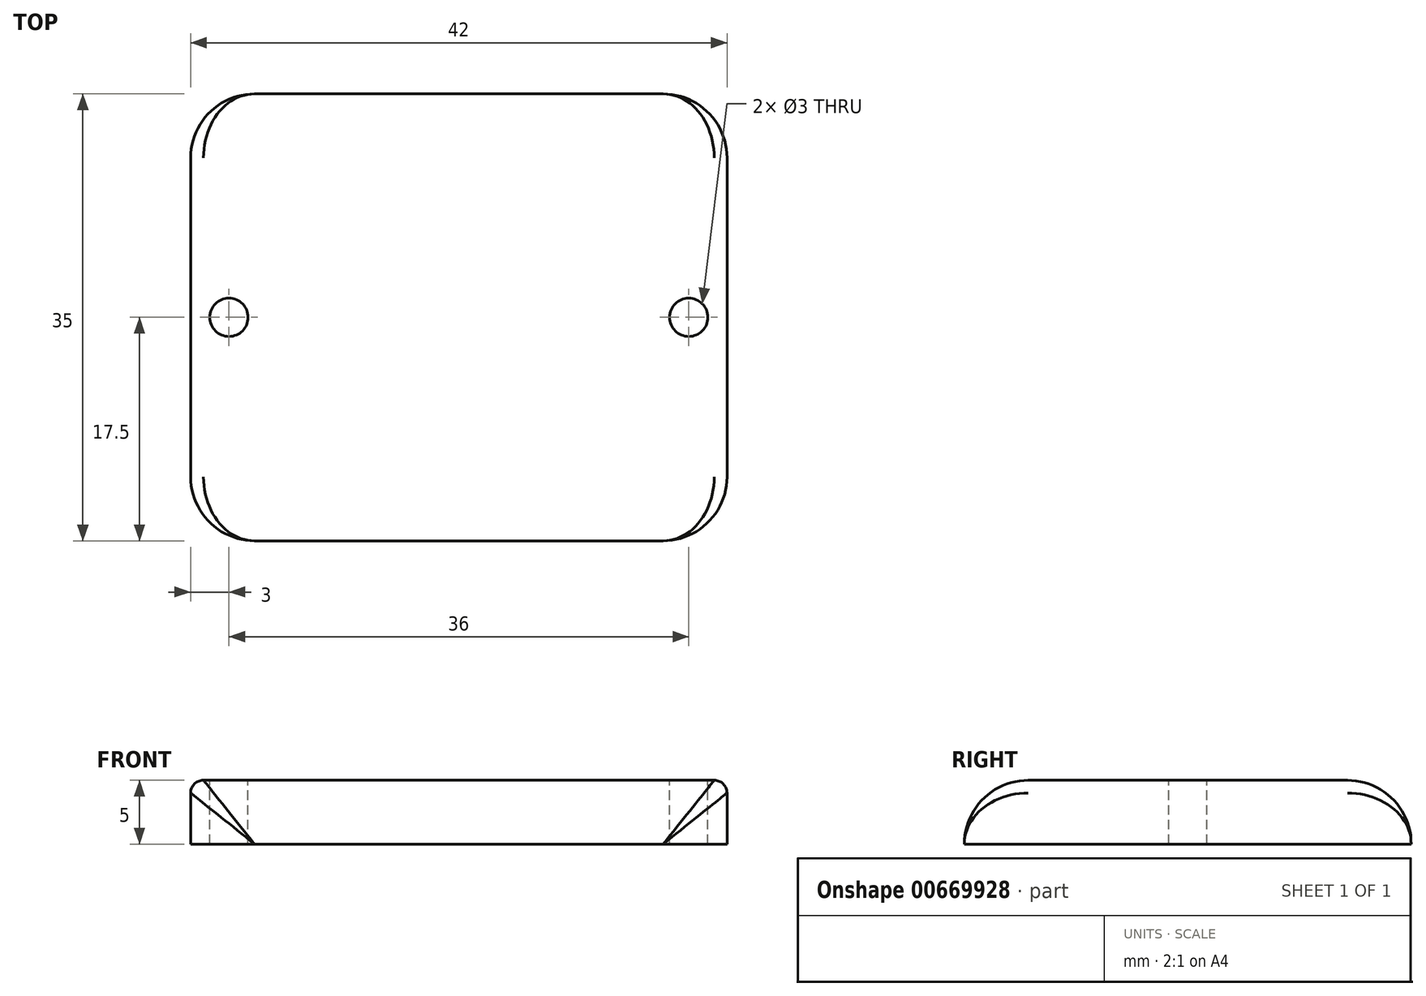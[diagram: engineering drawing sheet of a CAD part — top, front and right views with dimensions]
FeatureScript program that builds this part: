
annotation { "Feature Type Name" : "Feature", "Feature Type Description" : "" }
export const myFeature = defineFeature(function(context is Context, id is Id, definition is map)
    precondition{}
    {
        {
            var Q0;
            Q0=qCreatedBy(makeId("Top.planeOp"),FACE);
            var sketch = newSketch(context, id + "F0", { "sketchPlane" : qUnion([Q0])});
            skLineSegment(sketch, "E0.bottom", {"start": v(-21, 17.5) * mm, "end": v(21, 17.5) * mm});
            skLineSegment(sketch, "E0.top", {"start": v(-21, -17.5) * mm, "end": v(21, -17.5) * mm});
            skLineSegment(sketch, "E0.left", {"start": v(-21, 17.5) * mm, "end": v(-21, -17.5) * mm});
            skLineSegment(sketch, "E0.right", {"start": v(21, 17.5) * mm, "end": v(21, -17.5) * mm});
            skSolve(sketch);
        }
        {
            var Q0;
            Q0=makeQuery(id+"F0.imprint","IMPRINT",FACE,{"disambiguationData":[TD([[makeQuery(id+"F0.imprint","IMPRINT",EDGE,{"derivedFrom":sQuery(id+"F0.wireOp",EDGE,"E0.bottom")}),-1.0]])]});
            extrude(context, id + "F1", {"entities" : qUnion([Q0]), "depth" : 5 * mm, "offsetDistance" : 25 * mm});
        }
        {
            var Q0;
            Q0=makeQuery(id+"F1.opExtrude","SWEPT_EDGE",EDGE,{"disambiguationData":[OSD([sQuery(id+"F0.wireOp",EDGE,"E0.top"),sQuery(id+"F0.wireOp",EDGE,"E0.left")])]});
            var Q1;
            Q1=makeQuery(id+"F1.opExtrude","SWEPT_EDGE",EDGE,{"disambiguationData":[OSD([sQuery(id+"F0.wireOp",EDGE,"E0.top"),sQuery(id+"F0.wireOp",EDGE,"E0.right")])]});
            var Q2;
            Q2=makeQuery(id+"F1.opExtrude","SWEPT_EDGE",EDGE,{"disambiguationData":[OSD([sQuery(id+"F0.wireOp",EDGE,"E0.bottom"),sQuery(id+"F0.wireOp",EDGE,"E0.left")])]});
            var Q3;
            Q3=makeQuery(id+"F1.opExtrude","SWEPT_EDGE",EDGE,{"disambiguationData":[OSD([sQuery(id+"F0.wireOp",EDGE,"E0.bottom"),sQuery(id+"F0.wireOp",EDGE,"E0.right")])]});
            var Q4;
            Q4=makeQuery(id+"F1.opExtrude","CAP_EDGE",EDGE,{"disambiguationData":[OSD([sQuery(id+"F0.wireOp",EDGE,"E0.bottom")])],"isStart":false});
            var Q5;
            Q5=makeQuery(id+"F1.opExtrude","CAP_EDGE",EDGE,{"disambiguationData":[OSD([sQuery(id+"F0.wireOp",EDGE,"E0.top")])],"isStart":false});
            fillet(context, id + "F2", {"entities" : qUnion([Q0, Q1, Q2, Q3, Q4, Q5]), "radius" : 5 * mm, "tangentPropagation" : true, "allowEdgeOverflow" : false});
        }
        {
            var Q0;
            Q0=makeQuery(id+"F1.opExtrude","CAP_FACE",FACE,{"disambiguationData":[OSD([sQuery(id+"F0.wireOp",EDGE,"E0.bottom"),sQuery(id+"F0.wireOp",EDGE,"E0.top"),sQuery(id+"F0.wireOp",EDGE,"E0.left"),sQuery(id+"F0.wireOp",EDGE,"E0.right")])],"isStart":false});
            var sketch = newSketch(context, id + "F3", { "sketchPlane" : qUnion([Q0])});
            skCircle(sketch, "E1", {"center": v(-18, 0) * mm, "radius": 1.5 * mm});
            skCircle(sketch, "E2", {"center": v(18, 0) * mm, "radius": 1.5 * mm});
            skSolve(sketch);
        }
        {
            var Q0;
            Q0 = qSketchRegion(id + "F3", true);
            extrude(context, id + "F4", {"entities" : qUnion([Q0]), "operationType" : NewBodyOperationType.REMOVE, "oppositeDirection" : true, "depth" : 6 * mm, "offsetDistance" : 25 * mm});
        }
        {
            var Q0;
            Q0=makeQuery(id+"F1.opExtrude","CAP_EDGE",EDGE,{"disambiguationData":[OSD([sQuery(id+"F0.wireOp",EDGE,"E0.left")])],"isStart":false});
            var Q1;
            Q1=makeQuery(id+"F1.opExtrude","CAP_EDGE",EDGE,{"disambiguationData":[OSD([sQuery(id+"F0.wireOp",EDGE,"E0.right")])],"isStart":false});
            fillet(context, id + "F5", {"entities" : qUnion([Q0, Q1]), "radius" : 1 * mm, "tangentPropagation" : true, "allowEdgeOverflow" : false});
        }
    });
